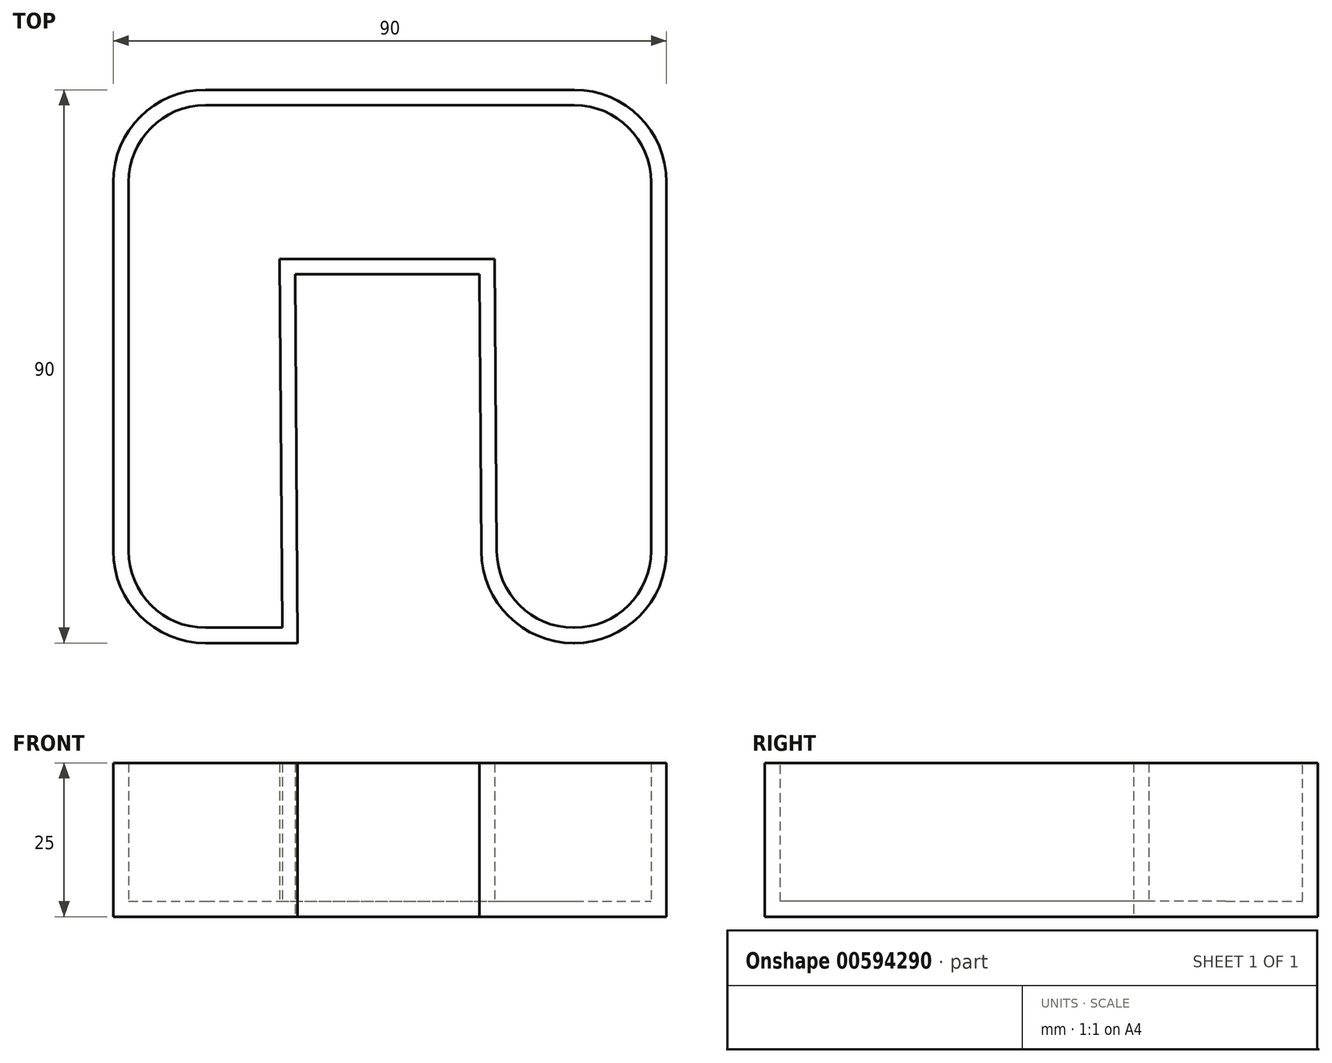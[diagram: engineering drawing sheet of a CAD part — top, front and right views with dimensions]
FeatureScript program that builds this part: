
annotation { "Feature Type Name" : "Feature", "Feature Type Description" : "" }
export const myFeature = defineFeature(function(context is Context, id is Id, definition is map)
    precondition{}
    {
        {
            var Q0;
            Q0=qCreatedBy(makeId("Top.planeOp"),FACE);
            var sketch = newSketch(context, id + "F0", { "sketchPlane" : qUnion([Q0])});
            skLineSegment(sketch, "E0.bottom", {"start": v(-34.86, 51.76) * mm, "end": v(25.14, 51.76) * mm});
            skLineSegment(sketch, "E0.top", {"start": v(-34.86, -38.24) * mm, "end": v(-19.86, -38.24) * mm});
            skLineSegment(sketch, "E0.left", {"start": v(-49.86, 36.76) * mm, "end": v(-49.86, -23.24) * mm});
            skLineSegment(sketch, "E0.right", {"start": v(40.14, 36.76) * mm, "end": v(40.14, -23.24) * mm});
            skLineSegment(sketch, "E1.bottom", {"start": v(-20.27, 21.76) * mm, "end": v(9.73, 21.76) * mm});
            skLineSegment(sketch, "E1.left", {"start": v(-20.27, 21.76) * mm, "end": v(-19.86, -38.24) * mm});
            skLineSegment(sketch, "E1.right", {"start": v(9.73, 21.76) * mm, "end": v(10.04, -23.34) * mm});
            skLineSegment(sketch, "E2.trimOffspring", {"start": v(25.04, -38.24) * mm, "end": v(25.14, -38.24) * mm});
            skPoint(sketch, "E3.visualSharp", {"position": v(-49.86, -38.24) * mm});
            skArc(sketch, "E3.filletArc", {"start": v(-49.86, -23.24) * mm, "mid": v(-45.47, -33.85) * mm, "end": v(-34.86, -38.24) * mm});
            skPoint(sketch, "E4.visualSharp", {"position": v(10.14, -38.24) * mm});
            skArc(sketch, "E4.filletArc", {"start": v(10.04, -23.34) * mm, "mid": v(14.47, -33.88) * mm, "end": v(25.04, -38.24) * mm});
            skPoint(sketch, "E5.visualSharp", {"position": v(-49.86, 51.76) * mm});
            skArc(sketch, "E5.filletArc", {"start": v(-34.86, 51.76) * mm, "mid": v(-45.47, 47.37) * mm, "end": v(-49.86, 36.76) * mm});
            skPoint(sketch, "E6.visualSharp", {"position": v(40.14, 51.76) * mm});
            skArc(sketch, "E6.filletArc", {"start": v(40.14, 36.76) * mm, "mid": v(35.74, 47.37) * mm, "end": v(25.14, 51.76) * mm});
            skPoint(sketch, "E7.visualSharp", {"position": v(40.14, -38.24) * mm});
            skArc(sketch, "E7.filletArc", {"start": v(25.14, -38.24) * mm, "mid": v(35.74, -33.85) * mm, "end": v(40.14, -23.24) * mm});
            skSolve(sketch);
        }
        {
            var Q0;
            Q0=makeQuery(id+"F0.imprint","IMPRINT",FACE,{"disambiguationData":[TD([[makeQuery(id+"F0.imprint","IMPRINT",EDGE,{"derivedFrom":sQuery(id+"F0.wireOp",EDGE,"E0.bottom")}),-1.0]])]});
            extrude(context, id + "F1", {"entities" : qUnion([Q0]), "depth" : 25 * mm, "offsetDistance" : 25 * mm});
        }
        {
            var Q0;
            Q0=makeQuery(id+"F1.opExtrude","CAP_FACE",FACE,{"disambiguationData":[OSD([sQuery(id+"F0.wireOp",EDGE,"E0.bottom"),sQuery(id+"F0.wireOp",EDGE,"E0.top"),sQuery(id+"F0.wireOp",EDGE,"E0.left"),sQuery(id+"F0.wireOp",EDGE,"E0.right"),sQuery(id+"F0.wireOp",EDGE,"E1.bottom"),sQuery(id+"F0.wireOp",EDGE,"E1.left"),sQuery(id+"F0.wireOp",EDGE,"E1.right"),sQuery(id+"F0.wireOp",EDGE,"E2.trimOffspring"),sQuery(id+"F0.wireOp",EDGE,"E3.filletArc"),sQuery(id+"F0.wireOp",EDGE,"E4.filletArc"),sQuery(id+"F0.wireOp",EDGE,"E5.filletArc"),sQuery(id+"F0.wireOp",EDGE,"E6.filletArc"),sQuery(id+"F0.wireOp",EDGE,"E7.filletArc")])],"isStart":false});
            shell(context, id + "F2", {"entities" : qUnion([Q0]), "thickness" : 2.5 * mm});
        }
    });
